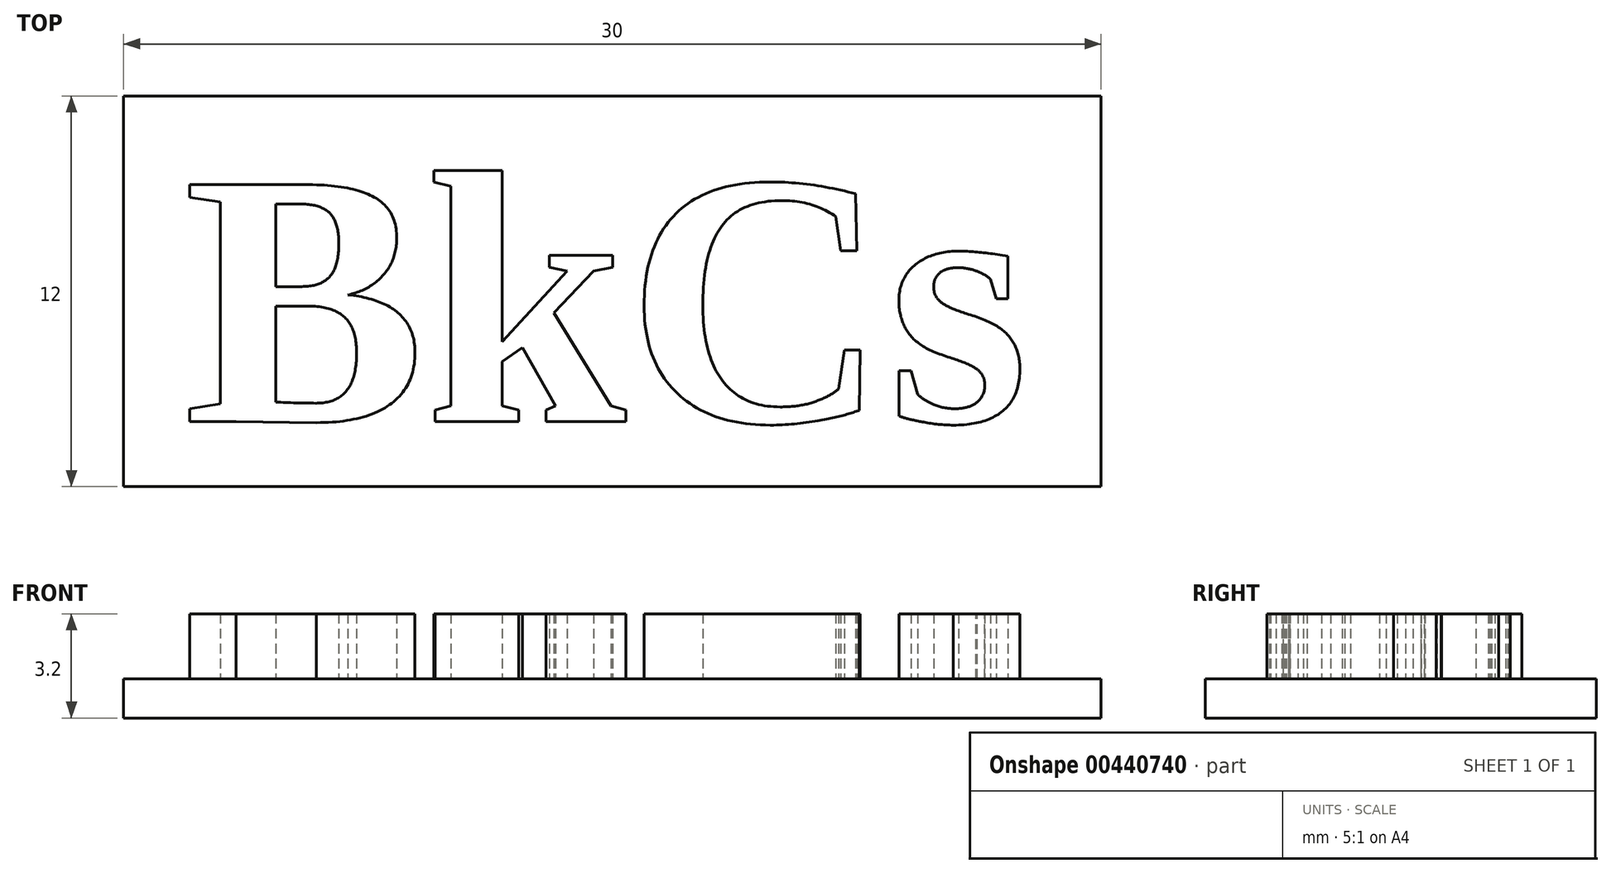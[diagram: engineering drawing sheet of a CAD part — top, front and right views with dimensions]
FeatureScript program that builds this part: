
annotation { "Feature Type Name" : "Feature", "Feature Type Description" : "" }
export const myFeature = defineFeature(function(context is Context, id is Id, definition is map)
    precondition{}
    {
        {
            var Q0;
            Q0=qCreatedBy(makeId("Top.planeOp"),FACE);
            var sketch = newSketch(context, id + "F0", { "sketchPlane" : qUnion([Q0])});
            skLineSegment(sketch, "E0.bottom", {"start": v(15, 6) * mm, "end": v(-15, 6) * mm});
            skLineSegment(sketch, "E0.top", {"start": v(15, -6) * mm, "end": v(-15, -6) * mm});
            skLineSegment(sketch, "E0.left", {"start": v(15, 6) * mm, "end": v(15, -6) * mm});
            skLineSegment(sketch, "E0.right", {"start": v(-15, 6) * mm, "end": v(-15, -6) * mm});
            skPoint(sketch, "E0.middle", {"position": v(0, 0) * mm});
            skSolve(sketch);
        }
        {
            var Q0;
            Q0=makeQuery(id+"F0.imprint","IMPRINT",FACE,{"disambiguationData":[TD([[makeQuery(id+"F0.imprint","IMPRINT",EDGE,{"derivedFrom":sQuery(id+"F0.wireOp",EDGE,"E0.bottom")}),1.0]])]});
            extrude(context, id + "F1", {"entities" : qUnion([Q0]), "depth" : 1.2 * mm});
        }
        {
            var Q0;
            Q0=makeQuery(id+"F1.opExtrude","CAP_FACE",FACE,{"disambiguationData":[OSD([sQuery(id+"F0.wireOp",EDGE,"E0.bottom"),sQuery(id+"F0.wireOp",EDGE,"E0.top"),sQuery(id+"F0.wireOp",EDGE,"E0.left"),sQuery(id+"F0.wireOp",EDGE,"E0.right")])],"isStart":false});
            var sketch = newSketch(context, id + "F2", { "sketchPlane" : qUnion([Q0])});
            skText(sketch, "E1", { "text": "BkCs", "fontName": "Tinos-Bold.ttf"});
            const initialGuessF2  = {"E1": [-0.01316, -0.004, 1, 0, 0.008]};
            skSetInitialGuess(sketch, initialGuessF2);
            skSolve(sketch);
        }
        {
            var Q0;
            Q0 = qSketchRegion(id + "F2", true);
            extrude(context, id + "F3", {"entities" : qUnion([Q0]), "operationType" : NewBodyOperationType.ADD, "depth" : 2 * mm});
        }
    });
